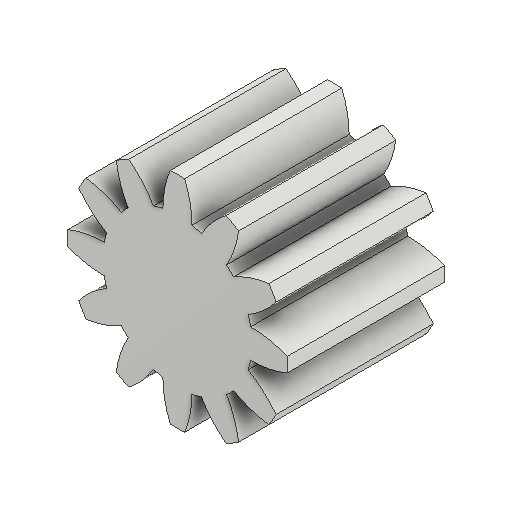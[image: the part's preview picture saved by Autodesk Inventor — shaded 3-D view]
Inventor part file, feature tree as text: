
AUTODESK INVENTOR PART (.ipt)
format: ipt  version: 2024 (Build 280153000, 153)  size: 221,696 bytes
history: native  units: mm (DEFAULTED — no unit token found)
features: plane x3, other x3, extrude x1, sketch x1
ambient origin geometry x8: Origin, YZ Plane, XZ Plane, XY Plane, X Axis, Y Axis, Z Axis, Center Point
bodies: Solid1 (feature_tree)
feature tree (8):
  extrude  "Extrusion1"  Depth=20.0mm TaperAngle=0.0deg
  plane  "Work Plane2"
  plane  "Work Plane8"
  plane  "Work Plane9"
  other  "Spur Gear"
  sketch  "Sketch1"  dims[d0=28.0mm d1=20.0mm d2=0.0mm d3=24.0mm d4=10.0mm d5=0.0mm d16=60.0mm d17=0.0mm d34=15.0deg d39=0.0mm d41=0.0mm d43=60.0mm d46=60.0mm d47=0.0mm d48=0.0mm]
  other  "Srf1"
  other  "Pitch Diameter"
